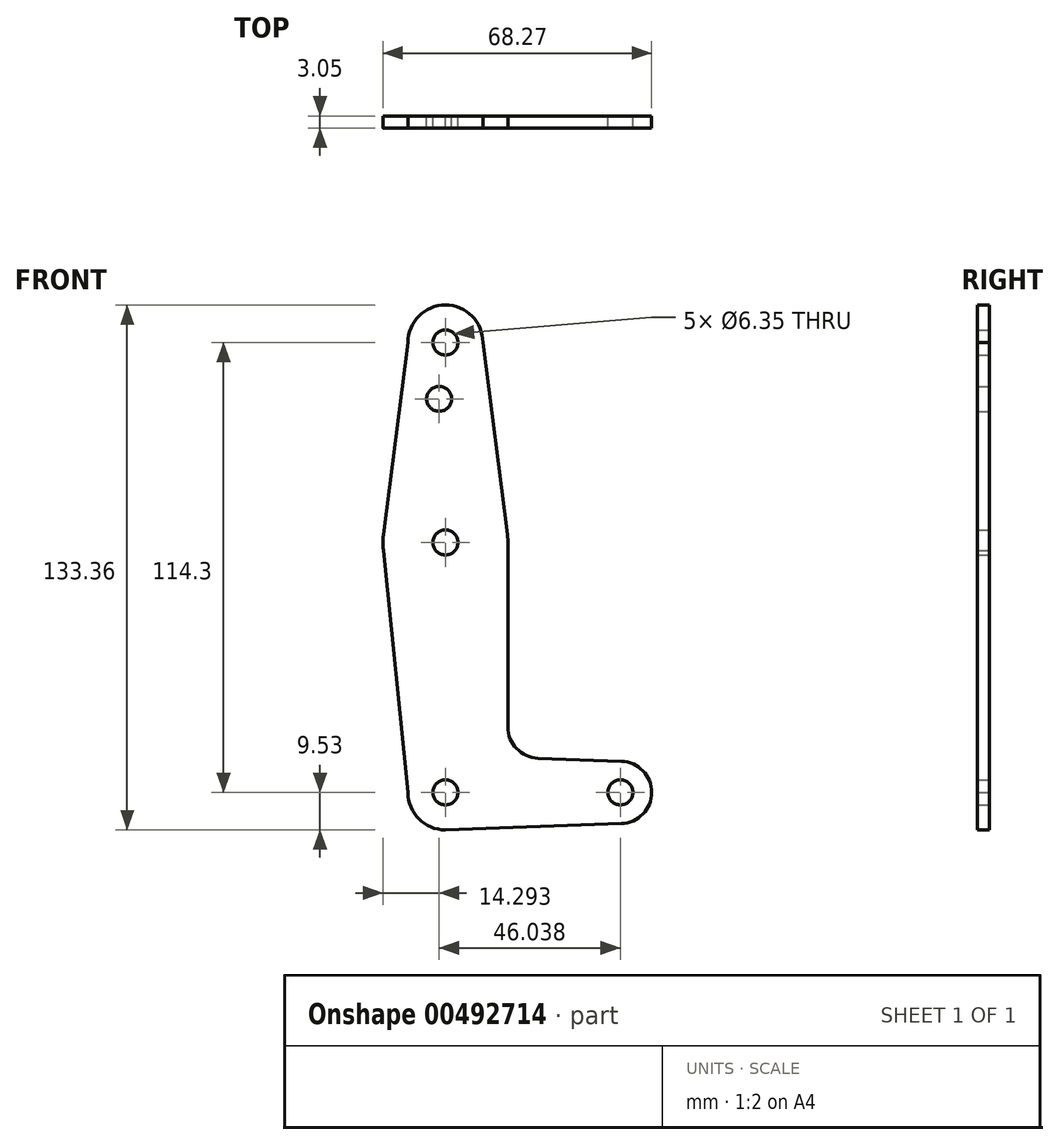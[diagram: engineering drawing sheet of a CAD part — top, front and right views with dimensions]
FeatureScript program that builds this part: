
annotation { "Feature Type Name" : "Feature", "Feature Type Description" : "" }
export const myFeature = defineFeature(function(context is Context, id is Id, definition is map)
    precondition{}
    {
        {
            var Q0;
            Q0=qCreatedBy(makeId("Front.planeOp"),FACE);
            var sketch = newSketch(context, id + "F0", { "sketchPlane" : qUnion([Q0])});
            skCircle(sketch, "E0", {"center": v(0, 0) * mm, "radius": 9.53 * mm});
            skCircle(sketch, "E1", {"center": v(44.45, 0) * mm, "radius": 7.94 * mm});
            skCircle(sketch, "E2", {"center": v(0, 63.5) * mm, "radius": 15.88 * mm});
            skCircle(sketch, "E3", {"center": v(0, 114.3) * mm, "radius": 9.53 * mm});
            skLineSegment(sketch, "E4", {"start": v(0, 114.3) * mm, "end": v(0, 0) * mm, "construction": true});
            skLineSegment(sketch, "E5", {"start": v(44.45, 0) * mm, "end": v(0, 0) * mm, "construction": true});
            skLineSegment(sketch, "E6", {"start": v(23.54, 8.69) * mm, "end": v(44.73, 7.93) * mm});
            skLineSegment(sketch, "E7", {"start": v(0, -9.53) * mm, "end": v(44.73, -7.93) * mm});
            skCircle(sketch, "E8", {"center": v(0, 114.3) * mm, "radius": 3.18 * mm});
            skCircle(sketch, "E9", {"center": v(-1.59, 100) * mm, "radius": 3.18 * mm});
            skCircle(sketch, "E10", {"center": v(0, 63.5) * mm, "radius": 3.18 * mm});
            skCircle(sketch, "E11", {"center": v(0, 0) * mm, "radius": 3.18 * mm});
            skLineSegment(sketch, "E12", {"start": v(9.52, 114.3) * mm, "end": v(15.75, 65.5) * mm});
            skLineSegment(sketch, "E13", {"start": v(-9.53, 114.3) * mm, "end": v(-15.75, 65.5) * mm});
            skLineSegment(sketch, "E14", {"start": v(15.88, 63.5) * mm, "end": v(15.88, 16.63) * mm});
            skLineSegment(sketch, "E15", {"start": v(-15.75, 61.5) * mm, "end": v(-9.52, 0) * mm});
            skCircle(sketch, "E16", {"center": v(44.45, 0) * mm, "radius": 3.18 * mm});
            skArc(sketch, "E17.filletArc", {"start": v(15.88, 16.63) * mm, "mid": v(18.1, 11.11) * mm, "end": v(23.54, 8.69) * mm});
            skSolve(sketch);
        }
        {
            var Q0;
            Q0=makeQuery(id+"F0.imprint","IMPRINT",FACE,{"disambiguationData":[TD([[makeQuery(id+"F0.imprint","IMPRINT",EDGE,{"derivedFrom":sQuery(id+"F0.wireOp",EDGE,"E9")}),-1.0]])]});
            var Q1;
            {var subQ0=sQuery(id+"F0.wireOp",EDGE,"E6");Q1=makeQuery(id+"F0.imprint","IMPRINT",FACE,{"disambiguationData":[TD([[makeQuery(id+"F0.imprint","IMPRINT",EDGE,{"derivedFrom":subQ0}),-1.0]])]});}
            var Q2;
            Q2=makeQuery(id+"F0.imprint","IMPRINT",FACE,{"disambiguationData":[TD([[makeQuery(id+"F0.imprint","IMPRINT",EDGE,{"derivedFrom":sQuery(id+"F0.wireOp",EDGE,"E10")}),-1.0]])]});
            var Q3;
            Q3=makeQuery(id+"F0.imprint","IMPRINT",FACE,{"disambiguationData":[TD([[makeQuery(id+"F0.imprint","IMPRINT",EDGE,{"derivedFrom":sQuery(id+"F0.wireOp",EDGE,"E8")}),-1.0]])]});
            var Q4;
            Q4=makeQuery(id+"F0.imprint","IMPRINT",FACE,{"disambiguationData":[TD([[makeQuery(id+"F0.imprint","IMPRINT",EDGE,{"derivedFrom":sQuery(id+"F0.wireOp",EDGE,"E11")}),-1.0]])]});
            var Q5;
            Q5=makeQuery(id+"F0.imprint","IMPRINT",FACE,{"disambiguationData":[TD([[makeQuery(id+"F0.imprint","IMPRINT",EDGE,{"derivedFrom":sQuery(id+"F0.wireOp",EDGE,"E16")}),-1.0]])]});
            extrude(context, id + "F1", {"entities" : qUnion([Q0, Q1, Q2, Q3, Q4, Q5]), "depth" : 3.05 * mm});
        }
    });
